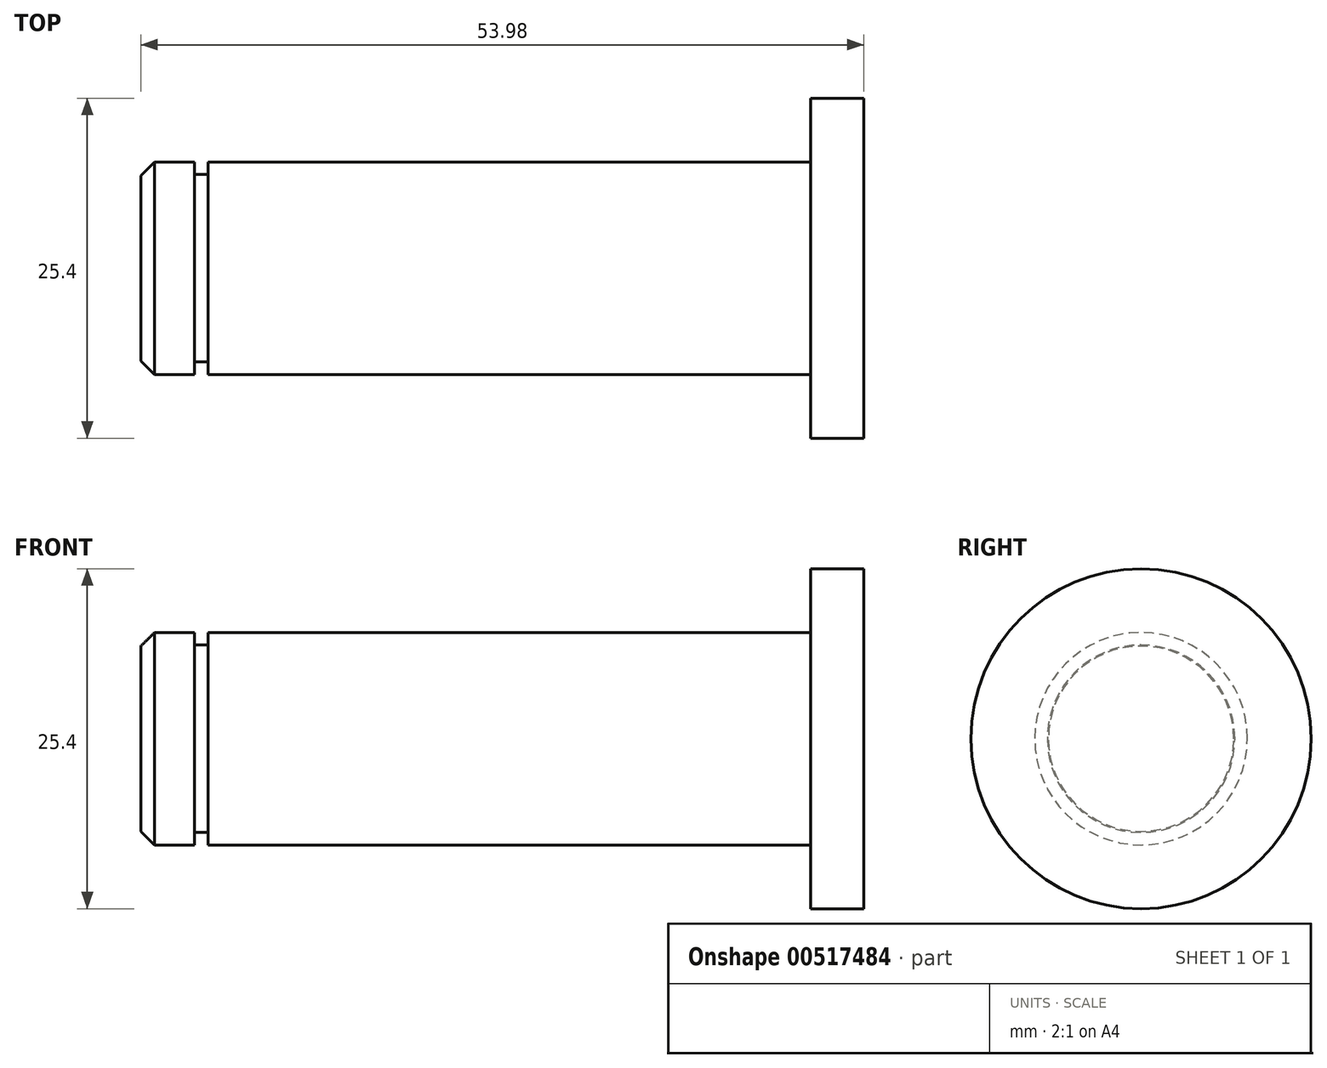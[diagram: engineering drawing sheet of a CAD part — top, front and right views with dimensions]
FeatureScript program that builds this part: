
annotation { "Feature Type Name" : "Feature", "Feature Type Description" : "" }
export const myFeature = defineFeature(function(context is Context, id is Id, definition is map)
    precondition{}
    {
        {
            var Q0;
            Q0=qCreatedBy(makeId("Front.planeOp"),FACE);
            var sketch = newSketch(context, id + "F0", { "sketchPlane" : qUnion([Q0])});
            skLineSegment(sketch, "E0", {"start": v(-13.15, 0) * mm, "end": v(-13.15, 7.94) * mm});
            skLineSegment(sketch, "E1", {"start": v(-13.15, 7.94) * mm, "end": v(-9.15, 7.94) * mm});
            skLineSegment(sketch, "E2", {"start": v(-9.15, 7.94) * mm, "end": v(-9.15, 7) * mm});
            skLineSegment(sketch, "E3", {"start": v(-9.15, 7) * mm, "end": v(-8.15, 7) * mm});
            skLineSegment(sketch, "E4", {"start": v(-8.15, 7) * mm, "end": v(-8.15, 7.94) * mm});
            skLineSegment(sketch, "E5", {"start": v(-8.15, 7.94) * mm, "end": v(36.86, 7.94) * mm});
            skLineSegment(sketch, "E6", {"start": v(36.86, 7.94) * mm, "end": v(36.86, 12.7) * mm});
            skLineSegment(sketch, "E7", {"start": v(36.86, 12.7) * mm, "end": v(40.83, 12.7) * mm});
            skLineSegment(sketch, "E8", {"start": v(40.83, 12.7) * mm, "end": v(40.83, 0) * mm});
            skLineSegment(sketch, "E9", {"start": v(-13.15, 0) * mm, "end": v(40.83, 0) * mm});
            skSolve(sketch);
        }
        {
            var Q0;
            Q0=qCreatedBy(makeId("Front.planeOp"),FACE);
            var sketch = newSketch(context, id + "F1", { "sketchPlane" : qUnion([Q0])});
            skLineSegment(sketch, "E10", {"start": v(-25.06, 0) * mm, "end": v(58.56, 0) * mm, "construction": true});
            skSolve(sketch);
        }
        {
            var Q0;
            Q0 = qSketchRegion(id + "F0", true);
            var Q1;
            Q1=sQuery(id+"F1.wireOp",EDGE,"E10");
            revolve(context, id + "F2", {"entities" : qUnion([Q0]), "axis" : qUnion([Q1]), "revolveType" : RevolveType.FULL});
        }
        {
            var Q0;
            Q0=makeQuery(id+"F2.opRevolve","SWEPT_EDGE",EDGE,{"disambiguationData":[OSD([sQuery(id+"F0.wireOp",EDGE,"E0"),sQuery(id+"F0.wireOp",EDGE,"E1")])]});
            chamfer(context, id + "F3", {"entities" : qUnion([Q0]), "width" : 1.02 * mm, "tangentPropagation" : true});
        }
    });
